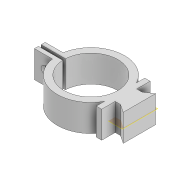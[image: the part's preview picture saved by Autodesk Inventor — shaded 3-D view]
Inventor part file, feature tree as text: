
AUTODESK INVENTOR PART (.ipt)
format: ipt  version: 2022 (Build 260153000, 153)  size: 312,320 bytes
history: native  units: mm
features: extrude x3, sketch x3, projected_geometry x3, plane x1
ambient origin geometry x8: Origin, YZ Plane, XZ Plane, XY Plane, X Axis, Y Axis, Z Axis, Center Point
bodies: Solid1 (feature_tree)
feature tree (10):
  extrude  "Extrusion1"  Depth=8.0mm
  plane  "Work Plane1"
  extrude  "Extrusion2"  Depth=2.0mm
  extrude  "Extrusion3"  Depth=2.0mm
  sketch  "Sketch1"  dims[d0=8.0mm d1=12.0mm]
  sketch  "Sketch2"  dims[d3=3.0mm d5=2.0mm]
  projected_geometry  "Projected Loop1"
  projected_geometry  "Projected Loop2"
  sketch  "Sketch3"  dims[d6=10.0mm d7=0.0mm d8=2.0mm d9=25.0mm d10=0.0mm d11=5.0mm d12=5.0mm d13=2.0mm d14=9.0mm d15=20.0mm d16=13.0mm d17=1.0mm d18=1.5mm d19=1.5mm d20=10.0mm d21=0.0mm d22=3.0mm d24=10.0mm d25=0.0mm d26=0.5mm d27=19.0mm d28=4.0mm]
  projected_geometry  "Projected Loop3"
